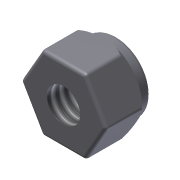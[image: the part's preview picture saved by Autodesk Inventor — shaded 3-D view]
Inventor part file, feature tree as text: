
AUTODESK INVENTOR PART (.ipt)
format: ipt  version: 2013 (Build 170138000, 138)  size: 182,784 bytes
history: native  units: in
note: dims shown in document units (in); Inventor stores cm internally (conversion verified against a paired STEP export)
features: sketch x5, extrude x3, fillet x2, hole x1, revolve x1, projected_geometry x1
ambient origin geometry x8: Origin, YZ Plane, XZ Plane, XY Plane, X Axis, Y Axis, Z Axis, Center Point
bodies: Solid1 (feature_tree)
feature tree (13):
  extrude  "Extrusion1"  Depth=0.25in TaperAngle=0.0deg
  extrude  "Extrusion2"  Depth=0.18in
  sketch  "Sketch8"  dims[d17=0.196in d18=0.172in d19=0.375in d20=0.25in d21=0.5635in d22=1.0in d23=0.8108in d24=0.18in]
  hole  "Hole2"  [1 undecoded]
  revolve  "Revolution2"  [1 undecoded]
  fillet  "Fillet1"  Radius=0.25in
  fillet  "Fillet2"  Radius=0.01in
  extrude  "Extrusion4"  [1 undecoded]
  sketch  "Sketch1"  dims[d0=0.4375in d1=0.25in d2=0.0in]
  sketch  "Sketch3"  dims[d4=0.0625in d5=0.0in]
  sketch  "Sketch9"  dims[d25=90.0deg d26=0.02in]
  sketch  "Sketch10"  dims[d27=0.02in d28=0.4in d29=0.25in d30=0.01in d31=0.0in]
  projected_geometry  "Projected Loop8"
note: 3 required parameter values undecoded (feature->parameter linkage not recoverable at this tier; creation-order binding heuristic only, values carry confidence <= 0.55)